# Revit family: SYSIMPLE FCC45A
name_source: partatom
category: Оборудование
units: mm (PartAtom-declared; Revit-internal decimal feet)

## family parameters
Всегда вертикально = Да
На основе рабочей плоскости = Нет
Общий = Нет
При загрузке вырезать с полостями = Нет
Размер круглого соединителя = Использовать диаметр
Тип детали = Нормальный
Точка расчета площади = Нет

## types (1)
- SYSIMPLE FCC45A
    Air guide size(mm) = /
    Body dimension(W) = 570×570×260
    COP = /
    Capacity = /
    Chassis height（mm) = /
    Compressor quantity = /
    Compressor type = /
    Cooling Power input = /
    Cooling capacity = 4500/3600/3060
    Cooling current = /
    Current of Circuit breaker = /
    Design Pressure(Mpa） = 1.6
    EER = /
    Fan motor quantity = /
    Front clearance(mm) = 1500 мм
    Gross Weight（body/panel） = 21/5
    Heating capacity = 6750/5940/5200
    Heating current = /
    Heating power input = /
    Inlet/Outlet /Drain  Water Pipe = DN20
    Installation hole spacing（L) = 510.4*514.6*530.5*463
    Installation hole spacing（W) = /
    Left Side clearance(ODU side mm) = /
    Manufacturer = AUX
    Manufacturer URL = /
    Max.Current input = /
    Max.Power input = /
    Model = AFC-500CA/4BA
    NET Weight（body/panel） = 18/3
    Noise Level(dB) = ≤45
    ODU fan ESP = /
    Operation range Heatling (°C） = /
    Operation range cooling (°C） = /
    Power = 220-240V,50,1
    Product series = Cassette FCU
    Protection grade = /
    Rear clearance(mm) = 1500 мм
    Refrigerant Charged Volume(kg) = /
    Refrigerant type = /
    Top clearance(mm) = 50 мм
    fan type = AC
    panel dimension(W) = 650x650x55
